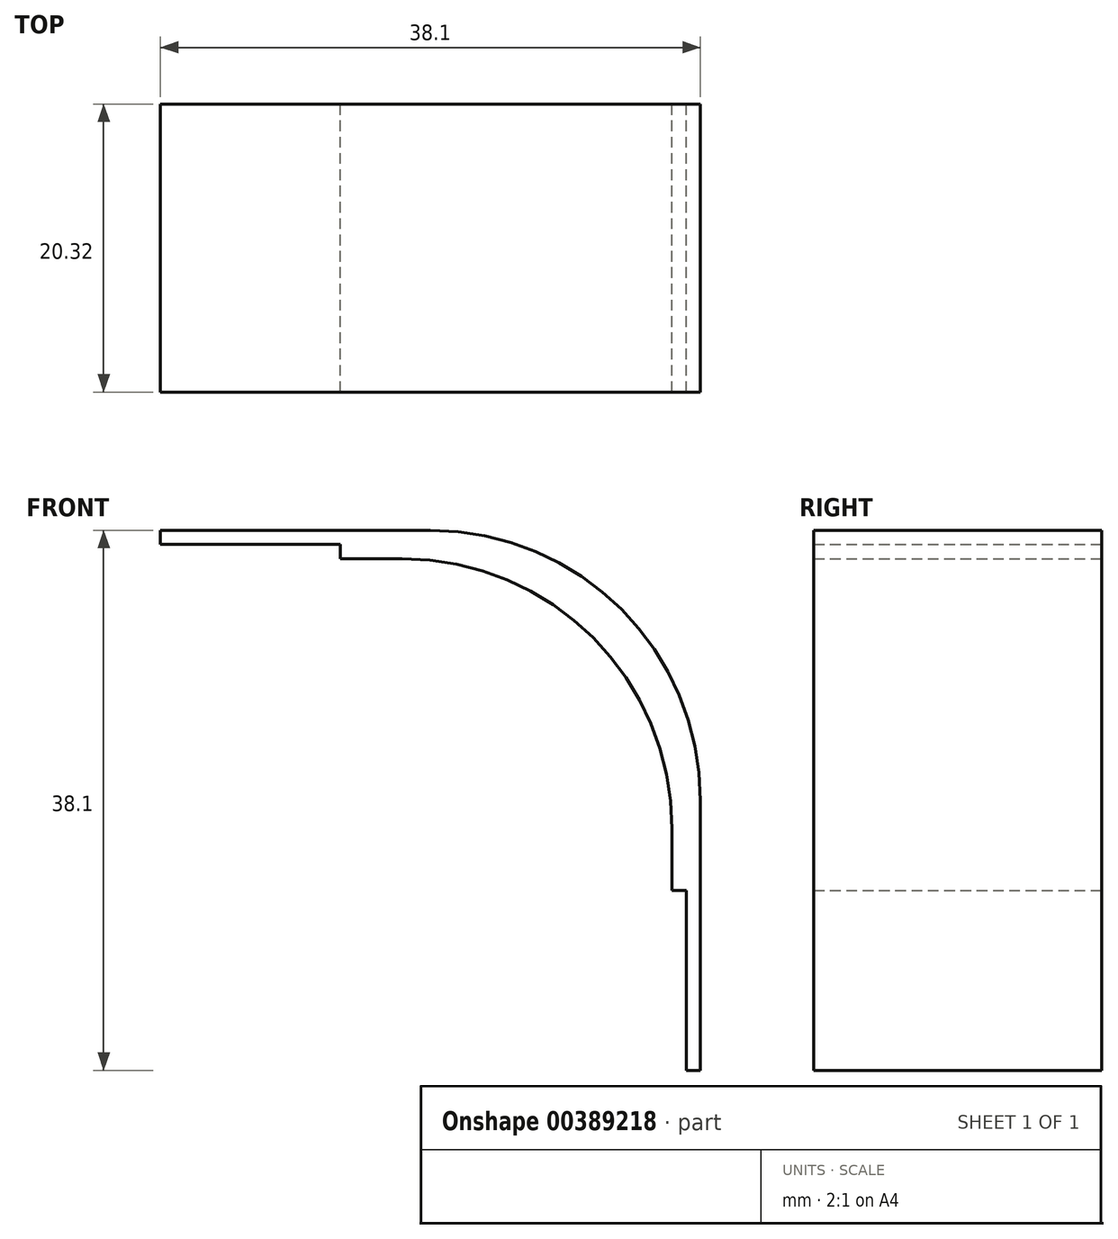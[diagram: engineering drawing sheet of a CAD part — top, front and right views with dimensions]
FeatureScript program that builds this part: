
annotation { "Feature Type Name" : "Feature", "Feature Type Description" : "" }
export const myFeature = defineFeature(function(context is Context, id is Id, definition is map)
    precondition{}
    {
        {
            var Q0;
            Q0=qCreatedBy(makeId("Front.planeOp"),FACE);
            var sketch = newSketch(context, id + "F0", { "sketchPlane" : qUnion([Q0])});
            skLineSegment(sketch, "E0", {"start": v(-3.87, 13.19) * mm, "end": v(2.48, 13.19) * mm});
            skLineSegment(sketch, "E1", {"start": v(21.53, -5.86) * mm, "end": v(21.53, -12.21) * mm});
            skLineSegment(sketch, "E2", {"start": v(19.53, -12.21) * mm, "end": v(19.53, -7.86) * mm});
            skLineSegment(sketch, "E3", {"start": v(0.48, 11.19) * mm, "end": v(-3.87, 11.19) * mm});
            skPoint(sketch, "E4.visualSharp", {"position": v(19.53, 11.19) * mm});
            skArc(sketch, "E4.filletArc", {"start": v(19.53, -7.86) * mm, "mid": v(13.95, 5.6) * mm, "end": v(0.48, 11.19) * mm});
            skPoint(sketch, "E5.visualSharp", {"position": v(21.53, 13.19) * mm});
            skArc(sketch, "E5.filletArc", {"start": v(21.53, -5.86) * mm, "mid": v(15.95, 7.6) * mm, "end": v(2.48, 13.19) * mm});
            skLineSegment(sketch, "E6", {"start": v(-3.87, 11.19) * mm, "end": v(-3.87, 12.19) * mm});
            skLineSegment(sketch, "E7", {"start": v(-3.87, 12.19) * mm, "end": v(-16.57, 12.19) * mm});
            skLineSegment(sketch, "E8", {"start": v(-16.57, 12.19) * mm, "end": v(-16.57, 13.19) * mm});
            skLineSegment(sketch, "E9", {"start": v(-16.57, 13.19) * mm, "end": v(-3.87, 13.19) * mm});
            skLineSegment(sketch, "E10", {"start": v(19.53, -12.21) * mm, "end": v(20.53, -12.21) * mm});
            skLineSegment(sketch, "E11", {"start": v(20.53, -12.21) * mm, "end": v(20.53, -24.91) * mm});
            skLineSegment(sketch, "E12", {"start": v(20.53, -24.91) * mm, "end": v(21.53, -24.91) * mm});
            skLineSegment(sketch, "E13", {"start": v(21.53, -24.91) * mm, "end": v(21.53, -12.21) * mm});
            skSolve(sketch);
        }
        {
            var Q0;
            Q0 = qSketchRegion(id + "F0", true);
            extrude(context, id + "F1", {"entities" : qUnion([Q0]), "depth" : 20.32 * mm, "offsetDistance" : 25.4 * mm});
        }
    });
